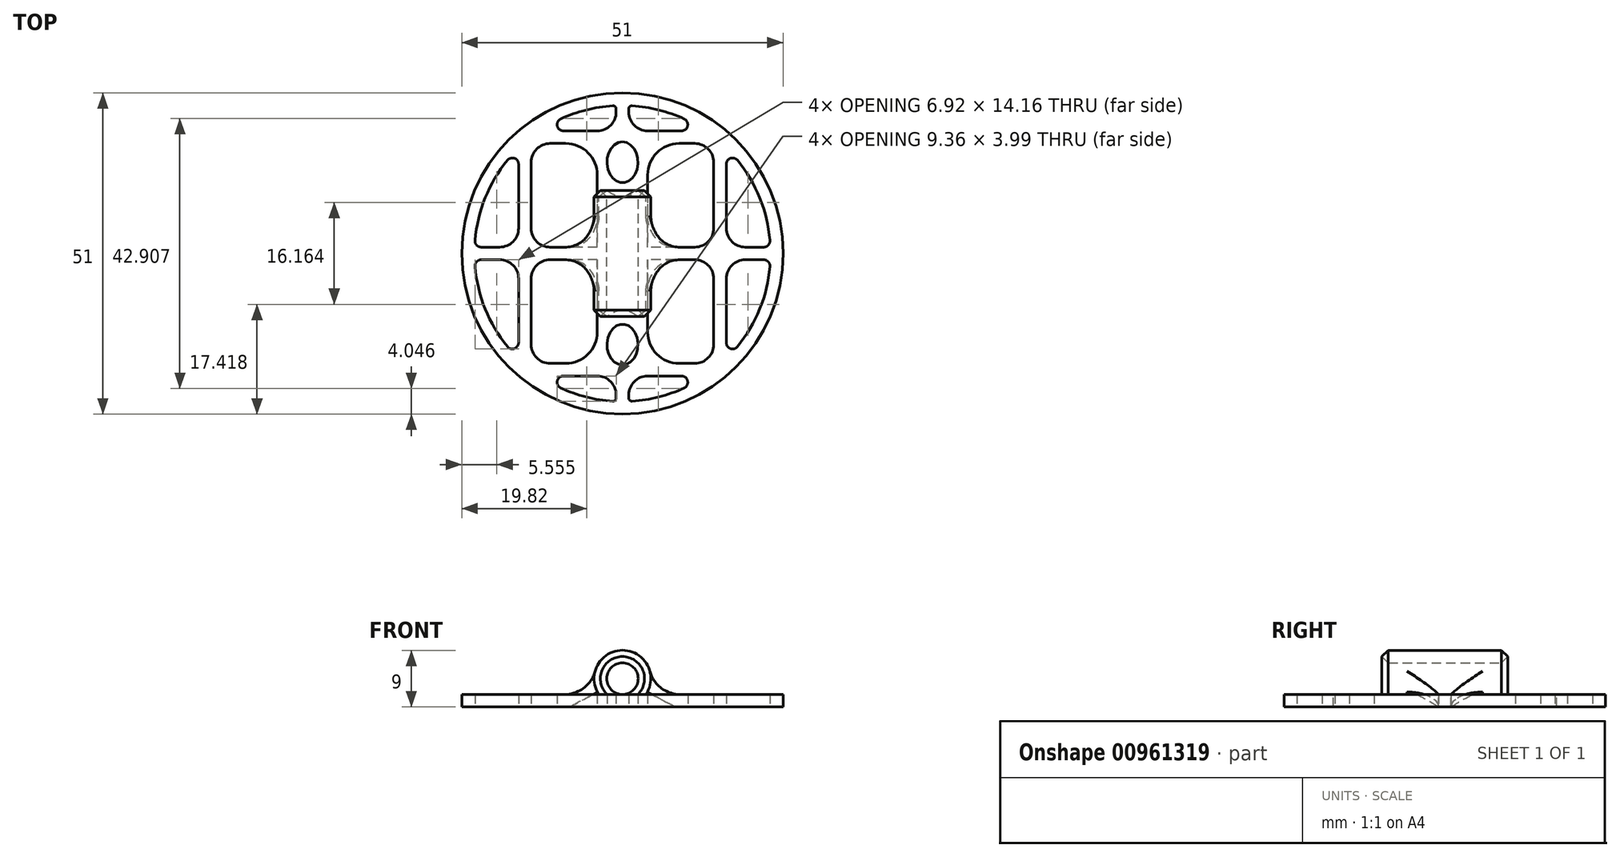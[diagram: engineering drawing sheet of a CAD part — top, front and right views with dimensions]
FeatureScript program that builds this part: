
annotation { "Feature Type Name" : "Feature", "Feature Type Description" : "" }
export const myFeature = defineFeature(function(context is Context, id is Id, definition is map)
    precondition{}
    {
        {
            var Q0;
            Q0=qCreatedBy(makeId("Top.planeOp"),FACE);
            var sketch = newSketch(context, id + "F0", { "sketchPlane" : qUnion([Q0])});
            skCircle(sketch, "E0", {"center": v(0, 0) * mm, "radius": 25.5 * mm});
            skArc(sketch, "E1.0", {"start": v(-18.26, 14.8) * mm, "mid": v(-21.78, 8.82) * mm, "end": v(-23.4, 2.09) * mm});
            skLineSegment(sketch, "E2.left", {"start": v(1, -22.95) * mm, "end": v(1, -22.46) * mm});
            skLineSegment(sketch, "E2.right", {"start": v(-1, -22.95) * mm, "end": v(-1, -22.46) * mm});
            skLineSegment(sketch, "E3.bottom", {"start": v(22.41, -1) * mm, "end": v(19.48, -1) * mm});
            skLineSegment(sketch, "E3.top", {"start": v(22.41, 1) * mm, "end": v(19.48, 1) * mm});
            skLineSegment(sketch, "E4.bottom", {"start": v(9.37, 19.46) * mm, "end": v(4, 19.46) * mm});
            skLineSegment(sketch, "E4.top", {"start": v(9.37, -19.46) * mm, "end": v(4, -19.46) * mm});
            skLineSegment(sketch, "E4.left", {"start": v(16.48, 14.16) * mm, "end": v(16.48, 4) * mm});
            skLineSegment(sketch, "E4.right", {"start": v(-16.48, 14.16) * mm, "end": v(-16.48, 4) * mm});
            skLineSegment(sketch, "E5.0", {"start": v(11.48, 17.46) * mm, "end": v(4, 17.46) * mm});
            skLineSegment(sketch, "E5.1", {"start": v(14.48, 14.46) * mm, "end": v(14.48, 4) * mm});
            skLineSegment(sketch, "E5.2", {"start": v(11.48, -17.46) * mm, "end": v(4, -17.46) * mm});
            skLineSegment(sketch, "E5.3", {"start": v(-14.48, 14.46) * mm, "end": v(-14.48, 4) * mm});
            skPoint(sketch, "E6.orphan", {"position": v(-16.48, 19.46) * mm});
            skArc(sketch, "E7.trimOffspring", {"start": v(-23.4, -2.09) * mm, "mid": v(-21.78, -8.82) * mm, "end": v(-18.26, -14.8) * mm});
            skLineSegment(sketch, "E8.trimOffspring", {"start": v(-16.48, -4) * mm, "end": v(-16.48, -14.16) * mm});
            skLineSegment(sketch, "E9.trimOffspring", {"start": v(-19.48, 1) * mm, "end": v(-22.41, 1) * mm});
            skLineSegment(sketch, "E10.trimOffspring", {"start": v(-19.48, -1) * mm, "end": v(-22.41, -1) * mm});
            skLineSegment(sketch, "E11.trimOffspring", {"start": v(-14.48, -4) * mm, "end": v(-14.48, -14.46) * mm});
            skLineSegment(sketch, "E12.trimOffspring", {"start": v(-1, 4) * mm, "end": v(-1, 14.46) * mm});
            skLineSegment(sketch, "E13.trimOffspring", {"start": v(-4, 1) * mm, "end": v(-11.48, 1) * mm});
            skLineSegment(sketch, "E14.trimOffspring", {"start": v(1, 4) * mm, "end": v(1, 14.46) * mm});
            skLineSegment(sketch, "E15.trimOffspring", {"start": v(-4, -1) * mm, "end": v(-11.48, -1) * mm});
            skLineSegment(sketch, "E16.trimOffspring", {"start": v(-4, 19.46) * mm, "end": v(-9.37, 19.46) * mm});
            skLineSegment(sketch, "E17.trimOffspring", {"start": v(-4, 17.46) * mm, "end": v(-11.48, 17.46) * mm});
            skArc(sketch, "E18.trimOffspring", {"start": v(-1.53, 23.45) * mm, "mid": v(-5.75, 22.78) * mm, "end": v(-9.78, 21.37) * mm});
            skPoint(sketch, "E19.orphan", {"position": v(16.48, 19.46) * mm});
            skArc(sketch, "E20.trimOffspring", {"start": v(9.78, 21.37) * mm, "mid": v(5.75, 22.78) * mm, "end": v(1.53, 23.45) * mm});
            skArc(sketch, "E21.trimOffspring", {"start": v(23.4, 2.09) * mm, "mid": v(21.78, 8.82) * mm, "end": v(18.26, 14.8) * mm});
            skLineSegment(sketch, "E22.trimOffspring", {"start": v(11.48, -1) * mm, "end": v(4, -1) * mm});
            skLineSegment(sketch, "E23.trimOffspring", {"start": v(14.48, -4) * mm, "end": v(14.48, -14.46) * mm});
            skLineSegment(sketch, "E24.trimOffspring", {"start": v(11.48, 1) * mm, "end": v(4, 1) * mm});
            skLineSegment(sketch, "E25.trimOffspring", {"start": v(16.48, -4) * mm, "end": v(16.48, -14.16) * mm});
            skLineSegment(sketch, "E26.trimOffspring", {"start": v(-4, -17.46) * mm, "end": v(-11.48, -17.46) * mm});
            skLineSegment(sketch, "E27.trimOffspring", {"start": v(-1, -14.46) * mm, "end": v(-1, -4) * mm});
            skLineSegment(sketch, "E28.trimOffspring", {"start": v(-4, -19.46) * mm, "end": v(-9.37, -19.46) * mm});
            skLineSegment(sketch, "E29.trimOffspring", {"start": v(1, -14.46) * mm, "end": v(1, -4) * mm});
            skArc(sketch, "E30.trimOffspring", {"start": v(1.53, -23.45) * mm, "mid": v(5.75, -22.78) * mm, "end": v(9.78, -21.37) * mm});
            skArc(sketch, "E31.trimOffspring", {"start": v(18.26, -14.8) * mm, "mid": v(21.78, -8.82) * mm, "end": v(23.4, -2.09) * mm});
            skPoint(sketch, "E32.orphan", {"position": v(16.48, -19.46) * mm});
            skArc(sketch, "E33.trimOffspring", {"start": v(-9.78, -21.37) * mm, "mid": v(-5.75, -22.78) * mm, "end": v(-1.53, -23.45) * mm});
            skPoint(sketch, "E34.orphan", {"position": v(-16.48, -19.46) * mm});
            skPoint(sketch, "E35.visualSharp", {"position": v(-14.48, -1) * mm});
            skArc(sketch, "E35.filletArc", {"start": v(-11.48, -1) * mm, "mid": v(-13.6, -1.88) * mm, "end": v(-14.48, -4) * mm});
            skPoint(sketch, "E36.visualSharp", {"position": v(-16.48, -1) * mm});
            skArc(sketch, "E36.filletArc", {"start": v(-16.48, -4) * mm, "mid": v(-17.36, -1.88) * mm, "end": v(-19.48, -1) * mm});
            skPoint(sketch, "E37.visualSharp", {"position": v(-16.48, 1) * mm});
            skArc(sketch, "E37.filletArc", {"start": v(-19.48, 1) * mm, "mid": v(-17.36, 1.88) * mm, "end": v(-16.48, 4) * mm});
            skPoint(sketch, "E38.visualSharp", {"position": v(-1, 1) * mm});
            skArc(sketch, "E38.filletArc", {"start": v(-4, 1) * mm, "mid": v(-1.88, 1.88) * mm, "end": v(-1, 4) * mm});
            skPoint(sketch, "E39.visualSharp", {"position": v(-14.48, -17.46) * mm});
            skArc(sketch, "E39.filletArc", {"start": v(-14.48, -14.46) * mm, "mid": v(-13.6, -16.58) * mm, "end": v(-11.48, -17.46) * mm});
            skPoint(sketch, "E40.visualSharp", {"position": v(-1, -17.46) * mm});
            skArc(sketch, "E40.filletArc", {"start": v(-4, -17.46) * mm, "mid": v(-1.88, -16.58) * mm, "end": v(-1, -14.46) * mm});
            skPoint(sketch, "E41.visualSharp", {"position": v(1, -17.46) * mm});
            skArc(sketch, "E41.filletArc", {"start": v(1, -14.46) * mm, "mid": v(1.88, -16.58) * mm, "end": v(4, -17.46) * mm});
            skPoint(sketch, "E42.visualSharp", {"position": v(1, -19.46) * mm});
            skArc(sketch, "E42.filletArc", {"start": v(4, -19.46) * mm, "mid": v(1.88, -20.34) * mm, "end": v(1, -22.46) * mm});
            skPoint(sketch, "E43.visualSharp", {"position": v(14.48, -17.46) * mm});
            skArc(sketch, "E43.filletArc", {"start": v(11.48, -17.46) * mm, "mid": v(13.6, -16.58) * mm, "end": v(14.48, -14.46) * mm});
            skPoint(sketch, "E44.visualSharp", {"position": v(1, -1) * mm});
            skArc(sketch, "E44.filletArc", {"start": v(4, -1) * mm, "mid": v(1.88, -1.88) * mm, "end": v(1, -4) * mm});
            skPoint(sketch, "E45.visualSharp", {"position": v(-1, -1) * mm});
            skArc(sketch, "E45.filletArc", {"start": v(-1, -4) * mm, "mid": v(-1.88, -1.88) * mm, "end": v(-4, -1) * mm});
            skPoint(sketch, "E46.visualSharp", {"position": v(1, 1) * mm});
            skArc(sketch, "E46.filletArc", {"start": v(1, 4) * mm, "mid": v(1.88, 1.88) * mm, "end": v(4, 1) * mm});
            skPoint(sketch, "E47.visualSharp", {"position": v(14.48, 1) * mm});
            skArc(sketch, "E47.filletArc", {"start": v(11.48, 1) * mm, "mid": v(13.6, 1.88) * mm, "end": v(14.48, 4) * mm});
            skPoint(sketch, "E48.visualSharp", {"position": v(14.48, -1) * mm});
            skArc(sketch, "E48.filletArc", {"start": v(14.48, -4) * mm, "mid": v(13.6, -1.88) * mm, "end": v(11.48, -1) * mm});
            skPoint(sketch, "E49.visualSharp", {"position": v(16.48, -1) * mm});
            skArc(sketch, "E49.filletArc", {"start": v(19.48, -1) * mm, "mid": v(17.36, -1.88) * mm, "end": v(16.48, -4) * mm});
            skPoint(sketch, "E50.visualSharp", {"position": v(16.48, 1) * mm});
            skArc(sketch, "E50.filletArc", {"start": v(16.48, 4) * mm, "mid": v(17.36, 1.88) * mm, "end": v(19.48, 1) * mm});
            skPoint(sketch, "E51.visualSharp", {"position": v(-14.48, 17.46) * mm});
            skArc(sketch, "E51.filletArc", {"start": v(-11.48, 17.46) * mm, "mid": v(-13.6, 16.58) * mm, "end": v(-14.48, 14.46) * mm});
            skPoint(sketch, "E52.visualSharp", {"position": v(-14.48, 1) * mm});
            skArc(sketch, "E52.filletArc", {"start": v(-14.48, 4) * mm, "mid": v(-13.6, 1.88) * mm, "end": v(-11.48, 1) * mm});
            skPoint(sketch, "E53.visualSharp", {"position": v(14.48, 17.46) * mm});
            skArc(sketch, "E53.filletArc", {"start": v(14.48, 14.46) * mm, "mid": v(13.6, 16.58) * mm, "end": v(11.48, 17.46) * mm});
            skPoint(sketch, "E54.visualSharp", {"position": v(-1, -19.46) * mm});
            skArc(sketch, "E54.filletArc", {"start": v(-1, -22.46) * mm, "mid": v(-1.88, -20.34) * mm, "end": v(-4, -19.46) * mm});
            skLineSegment(sketch, "E55.trimOffspring", {"start": v(-1, 22.46) * mm, "end": v(-1, 22.95) * mm});
            skLineSegment(sketch, "E56.trimOffspring", {"start": v(1, 22.46) * mm, "end": v(1, 22.95) * mm});
            skPoint(sketch, "E57.visualSharp", {"position": v(-1, 19.46) * mm});
            skArc(sketch, "E57.filletArc", {"start": v(-4, 19.46) * mm, "mid": v(-1.88, 20.34) * mm, "end": v(-1, 22.46) * mm});
            skPoint(sketch, "E58.visualSharp", {"position": v(-1, 17.46) * mm});
            skArc(sketch, "E58.filletArc", {"start": v(-1, 14.46) * mm, "mid": v(-1.88, 16.58) * mm, "end": v(-4, 17.46) * mm});
            skPoint(sketch, "E59.visualSharp", {"position": v(1, 17.46) * mm});
            skArc(sketch, "E59.filletArc", {"start": v(4, 17.46) * mm, "mid": v(1.88, 16.58) * mm, "end": v(1, 14.46) * mm});
            skPoint(sketch, "E60.visualSharp", {"position": v(1, 19.46) * mm});
            skArc(sketch, "E60.filletArc", {"start": v(1, 22.46) * mm, "mid": v(1.88, 20.34) * mm, "end": v(4, 19.46) * mm});
            skPoint(sketch, "E61.visualSharp", {"position": v(16.48, 16.75) * mm});
            skArc(sketch, "E61.filletArc", {"start": v(18.26, 14.8) * mm, "mid": v(17.15, 15.1) * mm, "end": v(16.48, 14.16) * mm});
            skPoint(sketch, "E62.visualSharp", {"position": v(23.48, 1) * mm});
            skArc(sketch, "E62.filletArc", {"start": v(22.41, 1) * mm, "mid": v(23.15, 1.33) * mm, "end": v(23.4, 2.09) * mm});
            skPoint(sketch, "E63.visualSharp", {"position": v(23.48, -1) * mm});
            skArc(sketch, "E63.filletArc", {"start": v(23.4, -2.09) * mm, "mid": v(23.15, -1.33) * mm, "end": v(22.41, -1) * mm});
            skPoint(sketch, "E64.visualSharp", {"position": v(16.48, -16.75) * mm});
            skArc(sketch, "E64.filletArc", {"start": v(16.48, -14.16) * mm, "mid": v(17.15, -15.1) * mm, "end": v(18.26, -14.8) * mm});
            skPoint(sketch, "E65.visualSharp", {"position": v(-16.48, -16.75) * mm});
            skArc(sketch, "E65.filletArc", {"start": v(-18.26, -14.8) * mm, "mid": v(-17.15, -15.1) * mm, "end": v(-16.48, -14.16) * mm});
            skPoint(sketch, "E66.visualSharp", {"position": v(-23.48, -1) * mm});
            skArc(sketch, "E66.filletArc", {"start": v(-22.41, -1) * mm, "mid": v(-23.15, -1.33) * mm, "end": v(-23.4, -2.09) * mm});
            skPoint(sketch, "E67.visualSharp", {"position": v(-23.48, 1) * mm});
            skArc(sketch, "E67.filletArc", {"start": v(-23.4, 2.09) * mm, "mid": v(-23.15, 1.33) * mm, "end": v(-22.41, 1) * mm});
            skPoint(sketch, "E68.visualSharp", {"position": v(-16.48, 16.75) * mm});
            skArc(sketch, "E68.filletArc", {"start": v(-16.48, 14.16) * mm, "mid": v(-17.15, 15.1) * mm, "end": v(-18.26, 14.8) * mm});
            skPoint(sketch, "E69.visualSharp", {"position": v(-13.18, 19.46) * mm});
            skArc(sketch, "E69.filletArc", {"start": v(-9.78, 21.37) * mm, "mid": v(-10.34, 20.24) * mm, "end": v(-9.37, 19.46) * mm});
            skPoint(sketch, "E70.visualSharp", {"position": v(13.18, 19.46) * mm});
            skArc(sketch, "E70.filletArc", {"start": v(9.37, 19.46) * mm, "mid": v(10.34, 20.24) * mm, "end": v(9.78, 21.37) * mm});
            skPoint(sketch, "E71.visualSharp", {"position": v(-13.18, -19.46) * mm});
            skArc(sketch, "E71.filletArc", {"start": v(-9.37, -19.46) * mm, "mid": v(-10.34, -20.24) * mm, "end": v(-9.78, -21.37) * mm});
            skPoint(sketch, "E72.visualSharp", {"position": v(13.18, -19.46) * mm});
            skArc(sketch, "E72.filletArc", {"start": v(9.78, -21.37) * mm, "mid": v(10.34, -20.24) * mm, "end": v(9.37, -19.46) * mm});
            skPoint(sketch, "E73.visualSharp", {"position": v(-1, 23.48) * mm});
            skArc(sketch, "E73.filletArc", {"start": v(-1, 22.95) * mm, "mid": v(-1.16, 23.32) * mm, "end": v(-1.53, 23.45) * mm});
            skPoint(sketch, "E74.visualSharp", {"position": v(1, 23.48) * mm});
            skArc(sketch, "E74.filletArc", {"start": v(1.53, 23.45) * mm, "mid": v(1.16, 23.32) * mm, "end": v(1, 22.95) * mm});
            skPoint(sketch, "E75.visualSharp", {"position": v(-1, -23.48) * mm});
            skArc(sketch, "E75.filletArc", {"start": v(-1.53, -23.45) * mm, "mid": v(-1.16, -23.32) * mm, "end": v(-1, -22.95) * mm});
            skPoint(sketch, "E76.visualSharp", {"position": v(1, -23.48) * mm});
            skArc(sketch, "E76.filletArc", {"start": v(1, -22.95) * mm, "mid": v(1.16, -23.32) * mm, "end": v(1.53, -23.45) * mm});
            skSolve(sketch);
        }
        {
            var Q0;
            Q0 = qSketchRegion(id + "F0", true);
            extrude(context, id + "F1", {"entities" : qUnion([Q0]), "depth" : 2 * mm, "offsetDistance" : 25 * mm});
        }
        {
            var Q0;
            Q0=qCreatedBy(makeId("Front.planeOp"),FACE);
            var sketch = newSketch(context, id + "F2", { "sketchPlane" : qUnion([Q0])});
            skCircle(sketch, "E77", {"center": v(0, 4.5) * mm, "radius": 2.5 * mm});
            skCircle(sketch, "E78.0", {"center": v(0, 4.5) * mm, "radius": 4.5 * mm});
            skSolve(sketch);
        }
        {
            var Q0;
            Q0=makeQuery(id+"F2.imprint","IMPRINT",FACE,{"disambiguationData":[TD([[makeQuery(id+"F2.imprint","IMPRINT",EDGE,{"derivedFrom":sQuery(id+"F2.wireOp",EDGE,"E77")}),-1.0]])]});
            extrude(context, id + "F3", {"entities" : qUnion([Q0]), "operationType" : NewBodyOperationType.ADD, "depth" : 10 * mm, "offsetDistance" : 25 * mm, "hasSecondDirection" : true, "secondDirectionOppositeDirection" : true, "secondDirectionDepth" : 10 * mm});
        }
        {
            var Q0;
            Q0=makeQuery(id+"F3.boolean.opBoolean","INTERSECT",EDGE,{"disambiguationData":[OD(0.0)],"derivedFrom":[makeQuery(id+"F1.opExtrude","CAP_FACE",FACE,{"disambiguationData":[OSD([sQuery(id+"F0.wireOp",EDGE,"E0"),sQuery(id+"F0.wireOp",EDGE,"E1.0"),sQuery(id+"F0.wireOp",EDGE,"E2.left"),sQuery(id+"F0.wireOp",EDGE,"E2.right"),sQuery(id+"F0.wireOp",EDGE,"E3.bottom"),sQuery(id+"F0.wireOp",EDGE,"E3.top"),sQuery(id+"F0.wireOp",EDGE,"E4.bottom"),sQuery(id+"F0.wireOp",EDGE,"E4.top"),sQuery(id+"F0.wireOp",EDGE,"E4.left"),sQuery(id+"F0.wireOp",EDGE,"E4.right"),sQuery(id+"F0.wireOp",EDGE,"E5.0"),sQuery(id+"F0.wireOp",EDGE,"E5.1"),sQuery(id+"F0.wireOp",EDGE,"E5.2"),sQuery(id+"F0.wireOp",EDGE,"E5.3"),sQuery(id+"F0.wireOp",EDGE,"E7.trimOffspring"),sQuery(id+"F0.wireOp",EDGE,"E8.trimOffspring"),sQuery(id+"F0.wireOp",EDGE,"E9.trimOffspring"),sQuery(id+"F0.wireOp",EDGE,"E10.trimOffspring"),sQuery(id+"F0.wireOp",EDGE,"E11.trimOffspring"),sQuery(id+"F0.wireOp",EDGE,"E12.trimOffspring"),sQuery(id+"F0.wireOp",EDGE,"E13.trimOffspring"),sQuery(id+"F0.wireOp",EDGE,"E14.trimOffspring"),sQuery(id+"F0.wireOp",EDGE,"E15.trimOffspring"),sQuery(id+"F0.wireOp",EDGE,"E16.trimOffspring"),sQuery(id+"F0.wireOp",EDGE,"E17.trimOffspring"),sQuery(id+"F0.wireOp",EDGE,"E18.trimOffspring"),sQuery(id+"F0.wireOp",EDGE,"E20.trimOffspring"),sQuery(id+"F0.wireOp",EDGE,"E21.trimOffspring"),sQuery(id+"F0.wireOp",EDGE,"E22.trimOffspring"),sQuery(id+"F0.wireOp",EDGE,"E23.trimOffspring"),sQuery(id+"F0.wireOp",EDGE,"E24.trimOffspring"),sQuery(id+"F0.wireOp",EDGE,"E25.trimOffspring"),sQuery(id+"F0.wireOp",EDGE,"E26.trimOffspring"),sQuery(id+"F0.wireOp",EDGE,"E27.trimOffspring"),sQuery(id+"F0.wireOp",EDGE,"E28.trimOffspring"),sQuery(id+"F0.wireOp",EDGE,"E29.trimOffspring"),sQuery(id+"F0.wireOp",EDGE,"E30.trimOffspring"),sQuery(id+"F0.wireOp",EDGE,"E31.trimOffspring"),sQuery(id+"F0.wireOp",EDGE,"E33.trimOffspring"),sQuery(id+"F0.wireOp",EDGE,"E35.filletArc"),sQuery(id+"F0.wireOp",EDGE,"E36.filletArc"),sQuery(id+"F0.wireOp",EDGE,"E37.filletArc"),sQuery(id+"F0.wireOp",EDGE,"E38.filletArc"),sQuery(id+"F0.wireOp",EDGE,"E39.filletArc"),sQuery(id+"F0.wireOp",EDGE,"E40.filletArc"),sQuery(id+"F0.wireOp",EDGE,"E41.filletArc"),sQuery(id+"F0.wireOp",EDGE,"E42.filletArc"),sQuery(id+"F0.wireOp",EDGE,"E43.filletArc"),sQuery(id+"F0.wireOp",EDGE,"E44.filletArc"),sQuery(id+"F0.wireOp",EDGE,"E45.filletArc"),sQuery(id+"F0.wireOp",EDGE,"E46.filletArc"),sQuery(id+"F0.wireOp",EDGE,"E47.filletArc"),sQuery(id+"F0.wireOp",EDGE,"E48.filletArc"),sQuery(id+"F0.wireOp",EDGE,"E49.filletArc"),sQuery(id+"F0.wireOp",EDGE,"E50.filletArc"),sQuery(id+"F0.wireOp",EDGE,"E51.filletArc"),sQuery(id+"F0.wireOp",EDGE,"E52.filletArc"),sQuery(id+"F0.wireOp",EDGE,"E53.filletArc"),sQuery(id+"F0.wireOp",EDGE,"E54.filletArc"),sQuery(id+"F0.wireOp",EDGE,"E55.trimOffspring"),sQuery(id+"F0.wireOp",EDGE,"E56.trimOffspring"),sQuery(id+"F0.wireOp",EDGE,"E57.filletArc"),sQuery(id+"F0.wireOp",EDGE,"E58.filletArc"),sQuery(id+"F0.wireOp",EDGE,"E59.filletArc"),sQuery(id+"F0.wireOp",EDGE,"E60.filletArc"),sQuery(id+"F0.wireOp",EDGE,"E61.filletArc"),sQuery(id+"F0.wireOp",EDGE,"E62.filletArc"),sQuery(id+"F0.wireOp",EDGE,"E63.filletArc"),sQuery(id+"F0.wireOp",EDGE,"E64.filletArc"),sQuery(id+"F0.wireOp",EDGE,"E65.filletArc"),sQuery(id+"F0.wireOp",EDGE,"E66.filletArc"),sQuery(id+"F0.wireOp",EDGE,"E67.filletArc"),sQuery(id+"F0.wireOp",EDGE,"E68.filletArc"),sQuery(id+"F0.wireOp",EDGE,"E69.filletArc"),sQuery(id+"F0.wireOp",EDGE,"E70.filletArc"),sQuery(id+"F0.wireOp",EDGE,"E71.filletArc"),sQuery(id+"F0.wireOp",EDGE,"E72.filletArc"),sQuery(id+"F0.wireOp",EDGE,"E73.filletArc"),sQuery(id+"F0.wireOp",EDGE,"E74.filletArc"),sQuery(id+"F0.wireOp",EDGE,"E75.filletArc"),sQuery(id+"F0.wireOp",EDGE,"E76.filletArc")])],"isStart":false}),makeQuery(id+"F3.opExtrude","SWEPT_FACE",FACE,{"disambiguationData":[OSD([sQuery(id+"F2.wireOp",EDGE,"E78.0")])]})]});
            var Q1;
            Q1=makeQuery(id+"F3.boolean.opBoolean","INTERSECT",EDGE,{"disambiguationData":[OD(1.0)],"derivedFrom":[makeQuery(id+"F1.opExtrude","CAP_FACE",FACE,{"disambiguationData":[OSD([sQuery(id+"F0.wireOp",EDGE,"E0"),sQuery(id+"F0.wireOp",EDGE,"E1.0"),sQuery(id+"F0.wireOp",EDGE,"E2.left"),sQuery(id+"F0.wireOp",EDGE,"E2.right"),sQuery(id+"F0.wireOp",EDGE,"E3.bottom"),sQuery(id+"F0.wireOp",EDGE,"E3.top"),sQuery(id+"F0.wireOp",EDGE,"E4.bottom"),sQuery(id+"F0.wireOp",EDGE,"E4.top"),sQuery(id+"F0.wireOp",EDGE,"E4.left"),sQuery(id+"F0.wireOp",EDGE,"E4.right"),sQuery(id+"F0.wireOp",EDGE,"E5.0"),sQuery(id+"F0.wireOp",EDGE,"E5.1"),sQuery(id+"F0.wireOp",EDGE,"E5.2"),sQuery(id+"F0.wireOp",EDGE,"E5.3"),sQuery(id+"F0.wireOp",EDGE,"E7.trimOffspring"),sQuery(id+"F0.wireOp",EDGE,"E8.trimOffspring"),sQuery(id+"F0.wireOp",EDGE,"E9.trimOffspring"),sQuery(id+"F0.wireOp",EDGE,"E10.trimOffspring"),sQuery(id+"F0.wireOp",EDGE,"E11.trimOffspring"),sQuery(id+"F0.wireOp",EDGE,"E12.trimOffspring"),sQuery(id+"F0.wireOp",EDGE,"E13.trimOffspring"),sQuery(id+"F0.wireOp",EDGE,"E14.trimOffspring"),sQuery(id+"F0.wireOp",EDGE,"E15.trimOffspring"),sQuery(id+"F0.wireOp",EDGE,"E16.trimOffspring"),sQuery(id+"F0.wireOp",EDGE,"E17.trimOffspring"),sQuery(id+"F0.wireOp",EDGE,"E18.trimOffspring"),sQuery(id+"F0.wireOp",EDGE,"E20.trimOffspring"),sQuery(id+"F0.wireOp",EDGE,"E21.trimOffspring"),sQuery(id+"F0.wireOp",EDGE,"E22.trimOffspring"),sQuery(id+"F0.wireOp",EDGE,"E23.trimOffspring"),sQuery(id+"F0.wireOp",EDGE,"E24.trimOffspring"),sQuery(id+"F0.wireOp",EDGE,"E25.trimOffspring"),sQuery(id+"F0.wireOp",EDGE,"E26.trimOffspring"),sQuery(id+"F0.wireOp",EDGE,"E27.trimOffspring"),sQuery(id+"F0.wireOp",EDGE,"E28.trimOffspring"),sQuery(id+"F0.wireOp",EDGE,"E29.trimOffspring"),sQuery(id+"F0.wireOp",EDGE,"E30.trimOffspring"),sQuery(id+"F0.wireOp",EDGE,"E31.trimOffspring"),sQuery(id+"F0.wireOp",EDGE,"E33.trimOffspring"),sQuery(id+"F0.wireOp",EDGE,"E35.filletArc"),sQuery(id+"F0.wireOp",EDGE,"E36.filletArc"),sQuery(id+"F0.wireOp",EDGE,"E37.filletArc"),sQuery(id+"F0.wireOp",EDGE,"E38.filletArc"),sQuery(id+"F0.wireOp",EDGE,"E39.filletArc"),sQuery(id+"F0.wireOp",EDGE,"E40.filletArc"),sQuery(id+"F0.wireOp",EDGE,"E41.filletArc"),sQuery(id+"F0.wireOp",EDGE,"E42.filletArc"),sQuery(id+"F0.wireOp",EDGE,"E43.filletArc"),sQuery(id+"F0.wireOp",EDGE,"E44.filletArc"),sQuery(id+"F0.wireOp",EDGE,"E45.filletArc"),sQuery(id+"F0.wireOp",EDGE,"E46.filletArc"),sQuery(id+"F0.wireOp",EDGE,"E47.filletArc"),sQuery(id+"F0.wireOp",EDGE,"E48.filletArc"),sQuery(id+"F0.wireOp",EDGE,"E49.filletArc"),sQuery(id+"F0.wireOp",EDGE,"E50.filletArc"),sQuery(id+"F0.wireOp",EDGE,"E51.filletArc"),sQuery(id+"F0.wireOp",EDGE,"E52.filletArc"),sQuery(id+"F0.wireOp",EDGE,"E53.filletArc"),sQuery(id+"F0.wireOp",EDGE,"E54.filletArc"),sQuery(id+"F0.wireOp",EDGE,"E55.trimOffspring"),sQuery(id+"F0.wireOp",EDGE,"E56.trimOffspring"),sQuery(id+"F0.wireOp",EDGE,"E57.filletArc"),sQuery(id+"F0.wireOp",EDGE,"E58.filletArc"),sQuery(id+"F0.wireOp",EDGE,"E59.filletArc"),sQuery(id+"F0.wireOp",EDGE,"E60.filletArc"),sQuery(id+"F0.wireOp",EDGE,"E61.filletArc"),sQuery(id+"F0.wireOp",EDGE,"E62.filletArc"),sQuery(id+"F0.wireOp",EDGE,"E63.filletArc"),sQuery(id+"F0.wireOp",EDGE,"E64.filletArc"),sQuery(id+"F0.wireOp",EDGE,"E65.filletArc"),sQuery(id+"F0.wireOp",EDGE,"E66.filletArc"),sQuery(id+"F0.wireOp",EDGE,"E67.filletArc"),sQuery(id+"F0.wireOp",EDGE,"E68.filletArc"),sQuery(id+"F0.wireOp",EDGE,"E69.filletArc"),sQuery(id+"F0.wireOp",EDGE,"E70.filletArc"),sQuery(id+"F0.wireOp",EDGE,"E71.filletArc"),sQuery(id+"F0.wireOp",EDGE,"E72.filletArc"),sQuery(id+"F0.wireOp",EDGE,"E73.filletArc"),sQuery(id+"F0.wireOp",EDGE,"E74.filletArc"),sQuery(id+"F0.wireOp",EDGE,"E75.filletArc"),sQuery(id+"F0.wireOp",EDGE,"E76.filletArc")])],"isStart":false}),makeQuery(id+"F3.opExtrude","SWEPT_FACE",FACE,{"disambiguationData":[OSD([sQuery(id+"F2.wireOp",EDGE,"E78.0")])]})]});
            var Q2;
            Q2=makeQuery(id+"F3.boolean.opBoolean","INTERSECT",EDGE,{"derivedFrom":[makeQuery(id+"F1.opExtrude","SWEPT_FACE",FACE,{"disambiguationData":[OSD([sQuery(id+"F0.wireOp",EDGE,"E14.trimOffspring")])]}),makeQuery(id+"F3.opExtrude","CAP_FACE",FACE,{"disambiguationData":[OSD([sQuery(id+"F2.wireOp",EDGE,"E77"),sQuery(id+"F2.wireOp",EDGE,"E78.0")])],"isStart":true})]});
            var Q3;
            Q3=makeQuery(id+"F3.boolean.opBoolean","INTERSECT",EDGE,{"derivedFrom":[makeQuery(id+"F1.opExtrude","SWEPT_FACE",FACE,{"disambiguationData":[OSD([sQuery(id+"F0.wireOp",EDGE,"E12.trimOffspring")])]}),makeQuery(id+"F3.opExtrude","CAP_FACE",FACE,{"disambiguationData":[OSD([sQuery(id+"F2.wireOp",EDGE,"E77"),sQuery(id+"F2.wireOp",EDGE,"E78.0")])],"isStart":true})]});
            var Q4;
            Q4=makeQuery(id+"F3.boolean.opBoolean","INTERSECT",EDGE,{"derivedFrom":[makeQuery(id+"F1.opExtrude","SWEPT_FACE",FACE,{"disambiguationData":[OSD([sQuery(id+"F0.wireOp",EDGE,"E27.trimOffspring")])]}),makeQuery(id+"F3.opExtrude","CAP_FACE",FACE,{"disambiguationData":[OSD([sQuery(id+"F2.wireOp",EDGE,"E77"),sQuery(id+"F2.wireOp",EDGE,"E78.0")])],"isStart":false})]});
            var Q5;
            Q5=makeQuery(id+"F3.boolean.opBoolean","INTERSECT",EDGE,{"derivedFrom":[makeQuery(id+"F1.opExtrude","SWEPT_FACE",FACE,{"disambiguationData":[OSD([sQuery(id+"F0.wireOp",EDGE,"E29.trimOffspring")])]}),makeQuery(id+"F3.opExtrude","CAP_FACE",FACE,{"disambiguationData":[OSD([sQuery(id+"F2.wireOp",EDGE,"E77"),sQuery(id+"F2.wireOp",EDGE,"E78.0")])],"isStart":false})]});
            fillet(context, id + "F4", {"entities" : qUnion([Q0, Q1, Q2, Q3, Q4, Q5]), "radius" : 5 * mm, "tangentPropagation" : true, "allowEdgeOverflow" : false});
        }
        {
            var Q0;
            Q0=makeQuery(id+"F3.boolean.opBoolean","INTERSECT",EDGE,{"derivedFrom":[makeQuery(id+"F1.opExtrude","SWEPT_FACE",FACE,{"disambiguationData":[OSD([sQuery(id+"F0.wireOp",EDGE,"E38.filletArc")])]}),makeQuery(id+"F3.opExtrude","SWEPT_FACE",FACE,{"disambiguationData":[OSD([sQuery(id+"F2.wireOp",EDGE,"E78.0")])]})]});
            var Q1;
            Q1=makeQuery(id+"F3.boolean.opBoolean","INTERSECT",EDGE,{"derivedFrom":[makeQuery(id+"F1.opExtrude","SWEPT_FACE",FACE,{"disambiguationData":[OSD([sQuery(id+"F0.wireOp",EDGE,"E46.filletArc")])]}),makeQuery(id+"F3.opExtrude","SWEPT_FACE",FACE,{"disambiguationData":[OSD([sQuery(id+"F2.wireOp",EDGE,"E78.0")])]})]});
            var Q2;
            Q2=makeQuery(id+"F3.boolean.opBoolean","INTERSECT",EDGE,{"derivedFrom":[makeQuery(id+"F1.opExtrude","SWEPT_FACE",FACE,{"disambiguationData":[OSD([sQuery(id+"F0.wireOp",EDGE,"E45.filletArc")])]}),makeQuery(id+"F3.opExtrude","SWEPT_FACE",FACE,{"disambiguationData":[OSD([sQuery(id+"F2.wireOp",EDGE,"E78.0")])]})]});
            var Q3;
            Q3=makeQuery(id+"F3.boolean.opBoolean","INTERSECT",EDGE,{"derivedFrom":[makeQuery(id+"F1.opExtrude","SWEPT_FACE",FACE,{"disambiguationData":[OSD([sQuery(id+"F0.wireOp",EDGE,"E44.filletArc")])]}),makeQuery(id+"F3.opExtrude","SWEPT_FACE",FACE,{"disambiguationData":[OSD([sQuery(id+"F2.wireOp",EDGE,"E78.0")])]})]});
            fillet(context, id + "F5", {"entities" : qUnion([Q0, Q1, Q2, Q3]), "radius" : 5 * mm, "tangentPropagation" : true, "allowEdgeOverflow" : false});
        }
        {
            var Q0;
            Q0=makeQuery(id+"F3.opExtrude","CAP_EDGE",EDGE,{"disambiguationData":[OSD([sQuery(id+"F2.wireOp",EDGE,"E77")])],"isStart":false});
            var Q1;
            Q1=makeQuery(id+"F3.opExtrude","CAP_EDGE",EDGE,{"disambiguationData":[OSD([sQuery(id+"F2.wireOp",EDGE,"E77")])],"isStart":true});
            var Q2;
            Q2=makeQuery(id+"F3.opExtrude","CAP_EDGE",EDGE,{"disambiguationData":[OSD([sQuery(id+"F2.wireOp",EDGE,"E78.0")])],"isStart":true});
            var Q3;
            Q3=makeQuery(id+"F3.opExtrude","CAP_EDGE",EDGE,{"disambiguationData":[OSD([sQuery(id+"F2.wireOp",EDGE,"E78.0")])],"isStart":false});
            chamfer(context, id + "F6", {"entities" : qUnion([Q0, Q1, Q2, Q3]), "width" : 1 * mm, "tangentPropagation" : true});
        }
        {
            var Q0;
            Q0=makeQuery(id+"F1.opExtrude","CAP_FACE",FACE,{"disambiguationData":[OSD([sQuery(id+"F0.wireOp",EDGE,"E0"),sQuery(id+"F0.wireOp",EDGE,"E1.0"),sQuery(id+"F0.wireOp",EDGE,"E2.left"),sQuery(id+"F0.wireOp",EDGE,"E2.right"),sQuery(id+"F0.wireOp",EDGE,"E3.bottom"),sQuery(id+"F0.wireOp",EDGE,"E3.top"),sQuery(id+"F0.wireOp",EDGE,"E4.bottom"),sQuery(id+"F0.wireOp",EDGE,"E4.top"),sQuery(id+"F0.wireOp",EDGE,"E4.left"),sQuery(id+"F0.wireOp",EDGE,"E4.right"),sQuery(id+"F0.wireOp",EDGE,"E5.0"),sQuery(id+"F0.wireOp",EDGE,"E5.1"),sQuery(id+"F0.wireOp",EDGE,"E5.2"),sQuery(id+"F0.wireOp",EDGE,"E5.3"),sQuery(id+"F0.wireOp",EDGE,"E7.trimOffspring"),sQuery(id+"F0.wireOp",EDGE,"E8.trimOffspring"),sQuery(id+"F0.wireOp",EDGE,"E9.trimOffspring"),sQuery(id+"F0.wireOp",EDGE,"E10.trimOffspring"),sQuery(id+"F0.wireOp",EDGE,"E11.trimOffspring"),sQuery(id+"F0.wireOp",EDGE,"E12.trimOffspring"),sQuery(id+"F0.wireOp",EDGE,"E13.trimOffspring"),sQuery(id+"F0.wireOp",EDGE,"E14.trimOffspring"),sQuery(id+"F0.wireOp",EDGE,"E15.trimOffspring"),sQuery(id+"F0.wireOp",EDGE,"E16.trimOffspring"),sQuery(id+"F0.wireOp",EDGE,"E17.trimOffspring"),sQuery(id+"F0.wireOp",EDGE,"E18.trimOffspring"),sQuery(id+"F0.wireOp",EDGE,"E20.trimOffspring"),sQuery(id+"F0.wireOp",EDGE,"E21.trimOffspring"),sQuery(id+"F0.wireOp",EDGE,"E22.trimOffspring"),sQuery(id+"F0.wireOp",EDGE,"E23.trimOffspring"),sQuery(id+"F0.wireOp",EDGE,"E24.trimOffspring"),sQuery(id+"F0.wireOp",EDGE,"E25.trimOffspring"),sQuery(id+"F0.wireOp",EDGE,"E26.trimOffspring"),sQuery(id+"F0.wireOp",EDGE,"E27.trimOffspring"),sQuery(id+"F0.wireOp",EDGE,"E28.trimOffspring"),sQuery(id+"F0.wireOp",EDGE,"E29.trimOffspring"),sQuery(id+"F0.wireOp",EDGE,"E30.trimOffspring"),sQuery(id+"F0.wireOp",EDGE,"E31.trimOffspring"),sQuery(id+"F0.wireOp",EDGE,"E33.trimOffspring"),sQuery(id+"F0.wireOp",EDGE,"E35.filletArc"),sQuery(id+"F0.wireOp",EDGE,"E36.filletArc"),sQuery(id+"F0.wireOp",EDGE,"E37.filletArc"),sQuery(id+"F0.wireOp",EDGE,"E38.filletArc"),sQuery(id+"F0.wireOp",EDGE,"E39.filletArc"),sQuery(id+"F0.wireOp",EDGE,"E40.filletArc"),sQuery(id+"F0.wireOp",EDGE,"E41.filletArc"),sQuery(id+"F0.wireOp",EDGE,"E42.filletArc"),sQuery(id+"F0.wireOp",EDGE,"E43.filletArc"),sQuery(id+"F0.wireOp",EDGE,"E44.filletArc"),sQuery(id+"F0.wireOp",EDGE,"E45.filletArc"),sQuery(id+"F0.wireOp",EDGE,"E46.filletArc"),sQuery(id+"F0.wireOp",EDGE,"E47.filletArc"),sQuery(id+"F0.wireOp",EDGE,"E48.filletArc"),sQuery(id+"F0.wireOp",EDGE,"E49.filletArc"),sQuery(id+"F0.wireOp",EDGE,"E50.filletArc"),sQuery(id+"F0.wireOp",EDGE,"E51.filletArc"),sQuery(id+"F0.wireOp",EDGE,"E52.filletArc"),sQuery(id+"F0.wireOp",EDGE,"E53.filletArc"),sQuery(id+"F0.wireOp",EDGE,"E54.filletArc"),sQuery(id+"F0.wireOp",EDGE,"E55.trimOffspring"),sQuery(id+"F0.wireOp",EDGE,"E56.trimOffspring"),sQuery(id+"F0.wireOp",EDGE,"E57.filletArc"),sQuery(id+"F0.wireOp",EDGE,"E58.filletArc"),sQuery(id+"F0.wireOp",EDGE,"E59.filletArc"),sQuery(id+"F0.wireOp",EDGE,"E60.filletArc"),sQuery(id+"F0.wireOp",EDGE,"E61.filletArc"),sQuery(id+"F0.wireOp",EDGE,"E62.filletArc"),sQuery(id+"F0.wireOp",EDGE,"E63.filletArc"),sQuery(id+"F0.wireOp",EDGE,"E64.filletArc"),sQuery(id+"F0.wireOp",EDGE,"E65.filletArc"),sQuery(id+"F0.wireOp",EDGE,"E66.filletArc"),sQuery(id+"F0.wireOp",EDGE,"E67.filletArc"),sQuery(id+"F0.wireOp",EDGE,"E68.filletArc"),sQuery(id+"F0.wireOp",EDGE,"E69.filletArc"),sQuery(id+"F0.wireOp",EDGE,"E70.filletArc"),sQuery(id+"F0.wireOp",EDGE,"E71.filletArc"),sQuery(id+"F0.wireOp",EDGE,"E72.filletArc"),sQuery(id+"F0.wireOp",EDGE,"E73.filletArc"),sQuery(id+"F0.wireOp",EDGE,"E74.filletArc"),sQuery(id+"F0.wireOp",EDGE,"E75.filletArc"),sQuery(id+"F0.wireOp",EDGE,"E76.filletArc")])],"isStart":true});
            var sketch = newSketch(context, id + "F7", { "sketchPlane" : qUnion([Q0])});
            skLineSegment(sketch, "E79.bottom", {"start": v(-4, -17.46) * mm, "end": v(4, -17.46) * mm});
            skLineSegment(sketch, "E79.top", {"start": v(-4, 17.46) * mm, "end": v(4, 17.46) * mm});
            skLineSegment(sketch, "E79.left", {"start": v(-4, -17.46) * mm, "end": v(-4, 17.46) * mm});
            skLineSegment(sketch, "E79.right", {"start": v(4, -17.46) * mm, "end": v(4, 17.46) * mm});
            skPoint(sketch, "E79.middle", {"position": v(0, 0) * mm});
            skSolve(sketch);
        }
        {
            var Q0;
            Q0 = qSketchRegion(id + "F7", true);
            extrude(context, id + "F8", {"entities" : qUnion([Q0]), "operationType" : NewBodyOperationType.ADD, "endBound" : BoundingType.UP_TO_NEXT, "oppositeDirection" : true, "depth" : 25 * mm, "offsetDistance" : 25 * mm});
        }
        {
            var Q0;
            Q0 = qSketchRegion(id + "F7", true);
            var Q1;
            Q1=makeQuery(id+"F1.opExtrude","CAP_FACE",FACE,{"disambiguationData":[OSD([sQuery(id+"F0.wireOp",EDGE,"E0"),sQuery(id+"F0.wireOp",EDGE,"E1.0"),sQuery(id+"F0.wireOp",EDGE,"E2.left"),sQuery(id+"F0.wireOp",EDGE,"E2.right"),sQuery(id+"F0.wireOp",EDGE,"E3.bottom"),sQuery(id+"F0.wireOp",EDGE,"E3.top"),sQuery(id+"F0.wireOp",EDGE,"E4.bottom"),sQuery(id+"F0.wireOp",EDGE,"E4.top"),sQuery(id+"F0.wireOp",EDGE,"E4.left"),sQuery(id+"F0.wireOp",EDGE,"E4.right"),sQuery(id+"F0.wireOp",EDGE,"E5.0"),sQuery(id+"F0.wireOp",EDGE,"E5.1"),sQuery(id+"F0.wireOp",EDGE,"E5.2"),sQuery(id+"F0.wireOp",EDGE,"E5.3"),sQuery(id+"F0.wireOp",EDGE,"E7.trimOffspring"),sQuery(id+"F0.wireOp",EDGE,"E8.trimOffspring"),sQuery(id+"F0.wireOp",EDGE,"E9.trimOffspring"),sQuery(id+"F0.wireOp",EDGE,"E10.trimOffspring"),sQuery(id+"F0.wireOp",EDGE,"E11.trimOffspring"),sQuery(id+"F0.wireOp",EDGE,"E12.trimOffspring"),sQuery(id+"F0.wireOp",EDGE,"E13.trimOffspring"),sQuery(id+"F0.wireOp",EDGE,"E14.trimOffspring"),sQuery(id+"F0.wireOp",EDGE,"E15.trimOffspring"),sQuery(id+"F0.wireOp",EDGE,"E16.trimOffspring"),sQuery(id+"F0.wireOp",EDGE,"E17.trimOffspring"),sQuery(id+"F0.wireOp",EDGE,"E18.trimOffspring"),sQuery(id+"F0.wireOp",EDGE,"E20.trimOffspring"),sQuery(id+"F0.wireOp",EDGE,"E21.trimOffspring"),sQuery(id+"F0.wireOp",EDGE,"E22.trimOffspring"),sQuery(id+"F0.wireOp",EDGE,"E23.trimOffspring"),sQuery(id+"F0.wireOp",EDGE,"E24.trimOffspring"),sQuery(id+"F0.wireOp",EDGE,"E25.trimOffspring"),sQuery(id+"F0.wireOp",EDGE,"E26.trimOffspring"),sQuery(id+"F0.wireOp",EDGE,"E27.trimOffspring"),sQuery(id+"F0.wireOp",EDGE,"E28.trimOffspring"),sQuery(id+"F0.wireOp",EDGE,"E29.trimOffspring"),sQuery(id+"F0.wireOp",EDGE,"E30.trimOffspring"),sQuery(id+"F0.wireOp",EDGE,"E31.trimOffspring"),sQuery(id+"F0.wireOp",EDGE,"E33.trimOffspring"),sQuery(id+"F0.wireOp",EDGE,"E35.filletArc"),sQuery(id+"F0.wireOp",EDGE,"E36.filletArc"),sQuery(id+"F0.wireOp",EDGE,"E37.filletArc"),sQuery(id+"F0.wireOp",EDGE,"E38.filletArc"),sQuery(id+"F0.wireOp",EDGE,"E39.filletArc"),sQuery(id+"F0.wireOp",EDGE,"E40.filletArc"),sQuery(id+"F0.wireOp",EDGE,"E41.filletArc"),sQuery(id+"F0.wireOp",EDGE,"E42.filletArc"),sQuery(id+"F0.wireOp",EDGE,"E43.filletArc"),sQuery(id+"F0.wireOp",EDGE,"E44.filletArc"),sQuery(id+"F0.wireOp",EDGE,"E45.filletArc"),sQuery(id+"F0.wireOp",EDGE,"E46.filletArc"),sQuery(id+"F0.wireOp",EDGE,"E47.filletArc"),sQuery(id+"F0.wireOp",EDGE,"E48.filletArc"),sQuery(id+"F0.wireOp",EDGE,"E49.filletArc"),sQuery(id+"F0.wireOp",EDGE,"E50.filletArc"),sQuery(id+"F0.wireOp",EDGE,"E51.filletArc"),sQuery(id+"F0.wireOp",EDGE,"E52.filletArc"),sQuery(id+"F0.wireOp",EDGE,"E53.filletArc"),sQuery(id+"F0.wireOp",EDGE,"E54.filletArc"),sQuery(id+"F0.wireOp",EDGE,"E55.trimOffspring"),sQuery(id+"F0.wireOp",EDGE,"E56.trimOffspring"),sQuery(id+"F0.wireOp",EDGE,"E57.filletArc"),sQuery(id+"F0.wireOp",EDGE,"E58.filletArc"),sQuery(id+"F0.wireOp",EDGE,"E59.filletArc"),sQuery(id+"F0.wireOp",EDGE,"E60.filletArc"),sQuery(id+"F0.wireOp",EDGE,"E61.filletArc"),sQuery(id+"F0.wireOp",EDGE,"E62.filletArc"),sQuery(id+"F0.wireOp",EDGE,"E63.filletArc"),sQuery(id+"F0.wireOp",EDGE,"E64.filletArc"),sQuery(id+"F0.wireOp",EDGE,"E65.filletArc"),sQuery(id+"F0.wireOp",EDGE,"E66.filletArc"),sQuery(id+"F0.wireOp",EDGE,"E67.filletArc"),sQuery(id+"F0.wireOp",EDGE,"E68.filletArc"),sQuery(id+"F0.wireOp",EDGE,"E69.filletArc"),sQuery(id+"F0.wireOp",EDGE,"E70.filletArc"),sQuery(id+"F0.wireOp",EDGE,"E71.filletArc"),sQuery(id+"F0.wireOp",EDGE,"E72.filletArc"),sQuery(id+"F0.wireOp",EDGE,"E73.filletArc"),sQuery(id+"F0.wireOp",EDGE,"E74.filletArc"),sQuery(id+"F0.wireOp",EDGE,"E75.filletArc"),sQuery(id+"F0.wireOp",EDGE,"E76.filletArc")])],"isStart":false});
            extrude(context, id + "F9", {"entities" : qUnion([Q0]), "operationType" : NewBodyOperationType.ADD, "endBound" : BoundingType.UP_TO_SURFACE, "oppositeDirection" : true, "depth" : 25 * mm, "endBoundEntityFace" : qUnion([Q1]), "offsetDistance" : 25 * mm});
        }
        {
            var Q0;
            {var subQ0=sQuery(id+"F0.wireOp",EDGE,"E58.filletArc");var subQ1=sQuery(id+"F0.wireOp",EDGE,"E17.trimOffspring");Q0=makeQuery(id+"F9.boolean.opBoolean","MERGE",EDGE,{"derivedFrom":[makeQuery(id+"F1.opExtrude","SWEPT_EDGE",EDGE,{"disambiguationData":[OSD([subQ1,subQ0])]}),makeQuery(id+"F9.opExtrude","SWEPT_EDGE",EDGE,{"disambiguationData":[OSD([subQ1,subQ0,sQuery(id+"F7.wireOp",EDGE,"E79.bottom"),sQuery(id+"F7.wireOp",EDGE,"E79.left")])]})]});}
            var Q1;
            {var subQ0=sQuery(id+"F0.wireOp",EDGE,"E40.filletArc");var subQ1=sQuery(id+"F0.wireOp",EDGE,"E26.trimOffspring");Q1=makeQuery(id+"F9.boolean.opBoolean","MERGE",EDGE,{"derivedFrom":[makeQuery(id+"F1.opExtrude","SWEPT_EDGE",EDGE,{"disambiguationData":[OSD([subQ1,subQ0])]}),makeQuery(id+"F9.opExtrude","SWEPT_EDGE",EDGE,{"disambiguationData":[OSD([subQ1,subQ0,sQuery(id+"F7.wireOp",EDGE,"E79.top"),sQuery(id+"F7.wireOp",EDGE,"E79.left")])]})]});}
            var Q2;
            {var subQ0=sQuery(id+"F0.wireOp",EDGE,"E59.filletArc");var subQ1=sQuery(id+"F0.wireOp",EDGE,"E5.0");Q2=makeQuery(id+"F9.boolean.opBoolean","MERGE",EDGE,{"derivedFrom":[makeQuery(id+"F1.opExtrude","SWEPT_EDGE",EDGE,{"disambiguationData":[OSD([subQ1,subQ0])]}),makeQuery(id+"F9.opExtrude","SWEPT_EDGE",EDGE,{"disambiguationData":[OSD([subQ1,subQ0,sQuery(id+"F7.wireOp",EDGE,"E79.bottom"),sQuery(id+"F7.wireOp",EDGE,"E79.right")])]})]});}
            var Q3;
            {var subQ0=sQuery(id+"F0.wireOp",EDGE,"E41.filletArc");var subQ1=sQuery(id+"F0.wireOp",EDGE,"E5.2");Q3=makeQuery(id+"F9.boolean.opBoolean","MERGE",EDGE,{"derivedFrom":[makeQuery(id+"F1.opExtrude","SWEPT_EDGE",EDGE,{"disambiguationData":[OSD([subQ1,subQ0])]}),makeQuery(id+"F9.opExtrude","SWEPT_EDGE",EDGE,{"disambiguationData":[OSD([subQ1,subQ0,sQuery(id+"F7.wireOp",EDGE,"E79.top"),sQuery(id+"F7.wireOp",EDGE,"E79.right")])]})]});}
            fillet(context, id + "F10", {"entities" : qUnion([Q0, Q1, Q2, Q3]), "radius" : 5 * mm, "tangentPropagation" : true, "allowEdgeOverflow" : false});
        }
        {
            var Q0;
            Q0=makeQuery(id+"F9.boolean.opBoolean","MERGE",FACE,{"derivedFrom":[makeQuery(id+"F1.opExtrude","CAP_FACE",FACE,{"disambiguationData":[OSD([sQuery(id+"F0.wireOp",EDGE,"E0"),sQuery(id+"F0.wireOp",EDGE,"E1.0"),sQuery(id+"F0.wireOp",EDGE,"E2.left"),sQuery(id+"F0.wireOp",EDGE,"E2.right"),sQuery(id+"F0.wireOp",EDGE,"E3.bottom"),sQuery(id+"F0.wireOp",EDGE,"E3.top"),sQuery(id+"F0.wireOp",EDGE,"E4.bottom"),sQuery(id+"F0.wireOp",EDGE,"E4.top"),sQuery(id+"F0.wireOp",EDGE,"E4.left"),sQuery(id+"F0.wireOp",EDGE,"E4.right"),sQuery(id+"F0.wireOp",EDGE,"E5.0"),sQuery(id+"F0.wireOp",EDGE,"E5.1"),sQuery(id+"F0.wireOp",EDGE,"E5.2"),sQuery(id+"F0.wireOp",EDGE,"E5.3"),sQuery(id+"F0.wireOp",EDGE,"E7.trimOffspring"),sQuery(id+"F0.wireOp",EDGE,"E8.trimOffspring"),sQuery(id+"F0.wireOp",EDGE,"E9.trimOffspring"),sQuery(id+"F0.wireOp",EDGE,"E10.trimOffspring"),sQuery(id+"F0.wireOp",EDGE,"E11.trimOffspring"),sQuery(id+"F0.wireOp",EDGE,"E12.trimOffspring"),sQuery(id+"F0.wireOp",EDGE,"E13.trimOffspring"),sQuery(id+"F0.wireOp",EDGE,"E14.trimOffspring"),sQuery(id+"F0.wireOp",EDGE,"E15.trimOffspring"),sQuery(id+"F0.wireOp",EDGE,"E16.trimOffspring"),sQuery(id+"F0.wireOp",EDGE,"E17.trimOffspring"),sQuery(id+"F0.wireOp",EDGE,"E18.trimOffspring"),sQuery(id+"F0.wireOp",EDGE,"E20.trimOffspring"),sQuery(id+"F0.wireOp",EDGE,"E21.trimOffspring"),sQuery(id+"F0.wireOp",EDGE,"E22.trimOffspring"),sQuery(id+"F0.wireOp",EDGE,"E23.trimOffspring"),sQuery(id+"F0.wireOp",EDGE,"E24.trimOffspring"),sQuery(id+"F0.wireOp",EDGE,"E25.trimOffspring"),sQuery(id+"F0.wireOp",EDGE,"E26.trimOffspring"),sQuery(id+"F0.wireOp",EDGE,"E27.trimOffspring"),sQuery(id+"F0.wireOp",EDGE,"E28.trimOffspring"),sQuery(id+"F0.wireOp",EDGE,"E29.trimOffspring"),sQuery(id+"F0.wireOp",EDGE,"E30.trimOffspring"),sQuery(id+"F0.wireOp",EDGE,"E31.trimOffspring"),sQuery(id+"F0.wireOp",EDGE,"E33.trimOffspring"),sQuery(id+"F0.wireOp",EDGE,"E35.filletArc"),sQuery(id+"F0.wireOp",EDGE,"E36.filletArc"),sQuery(id+"F0.wireOp",EDGE,"E37.filletArc"),sQuery(id+"F0.wireOp",EDGE,"E38.filletArc"),sQuery(id+"F0.wireOp",EDGE,"E39.filletArc"),sQuery(id+"F0.wireOp",EDGE,"E40.filletArc"),sQuery(id+"F0.wireOp",EDGE,"E41.filletArc"),sQuery(id+"F0.wireOp",EDGE,"E42.filletArc"),sQuery(id+"F0.wireOp",EDGE,"E43.filletArc"),sQuery(id+"F0.wireOp",EDGE,"E44.filletArc"),sQuery(id+"F0.wireOp",EDGE,"E45.filletArc"),sQuery(id+"F0.wireOp",EDGE,"E46.filletArc"),sQuery(id+"F0.wireOp",EDGE,"E47.filletArc"),sQuery(id+"F0.wireOp",EDGE,"E48.filletArc"),sQuery(id+"F0.wireOp",EDGE,"E49.filletArc"),sQuery(id+"F0.wireOp",EDGE,"E50.filletArc"),sQuery(id+"F0.wireOp",EDGE,"E51.filletArc"),sQuery(id+"F0.wireOp",EDGE,"E52.filletArc"),sQuery(id+"F0.wireOp",EDGE,"E53.filletArc"),sQuery(id+"F0.wireOp",EDGE,"E54.filletArc"),sQuery(id+"F0.wireOp",EDGE,"E55.trimOffspring"),sQuery(id+"F0.wireOp",EDGE,"E56.trimOffspring"),sQuery(id+"F0.wireOp",EDGE,"E57.filletArc"),sQuery(id+"F0.wireOp",EDGE,"E58.filletArc"),sQuery(id+"F0.wireOp",EDGE,"E59.filletArc"),sQuery(id+"F0.wireOp",EDGE,"E60.filletArc"),sQuery(id+"F0.wireOp",EDGE,"E61.filletArc"),sQuery(id+"F0.wireOp",EDGE,"E62.filletArc"),sQuery(id+"F0.wireOp",EDGE,"E63.filletArc"),sQuery(id+"F0.wireOp",EDGE,"E64.filletArc"),sQuery(id+"F0.wireOp",EDGE,"E65.filletArc"),sQuery(id+"F0.wireOp",EDGE,"E66.filletArc"),sQuery(id+"F0.wireOp",EDGE,"E67.filletArc"),sQuery(id+"F0.wireOp",EDGE,"E68.filletArc"),sQuery(id+"F0.wireOp",EDGE,"E69.filletArc"),sQuery(id+"F0.wireOp",EDGE,"E70.filletArc"),sQuery(id+"F0.wireOp",EDGE,"E71.filletArc"),sQuery(id+"F0.wireOp",EDGE,"E72.filletArc"),sQuery(id+"F0.wireOp",EDGE,"E73.filletArc"),sQuery(id+"F0.wireOp",EDGE,"E74.filletArc"),sQuery(id+"F0.wireOp",EDGE,"E75.filletArc"),sQuery(id+"F0.wireOp",EDGE,"E76.filletArc")])],"isStart":false}),makeQuery(id+"F9.opExtrude","CAP_FACE",FACE,{"disambiguationData":[OSD([sQuery(id+"F7.wireOp",EDGE,"E79.bottom"),sQuery(id+"F7.wireOp",EDGE,"E79.top"),sQuery(id+"F7.wireOp",EDGE,"E79.left"),sQuery(id+"F7.wireOp",EDGE,"E79.right")])],"isStart":false})]});
            var sketch = newSketch(context, id + "F11", { "sketchPlane" : qUnion([Q0])});
            skLineSegment(sketch, "E80", {"start": v(0, 29.86) * mm, "end": v(0, -32.39) * mm, "construction": true});
            skLineSegment(sketch, "E81", {"start": v(15.7, 0) * mm, "end": v(-17.63, 0) * mm, "construction": true});
            skEllipse(sketch, "E82", {"center": v(0, 14.47) * mm, "majorRadius": 3.25 * mm, "minorRadius": 2.46 * mm, "majorAxis": v(0, 1)});
            skEllipse(sketch, "E83.MirrorC", {"center": v(0, -14.47) * mm, "majorRadius": 3.25 * mm, "minorRadius": 2.46 * mm, "majorAxis": v(0, -1)});
            skSolve(sketch);
        }
        {
            var Q0;
            Q0 = qSketchRegion(id + "F11", true);
            extrude(context, id + "F12", {"entities" : qUnion([Q0]), "operationType" : NewBodyOperationType.REMOVE, "endBound" : BoundingType.THROUGH_ALL, "oppositeDirection" : true, "depth" : 25 * mm, "offsetDistance" : 25 * mm});
        }
    });
